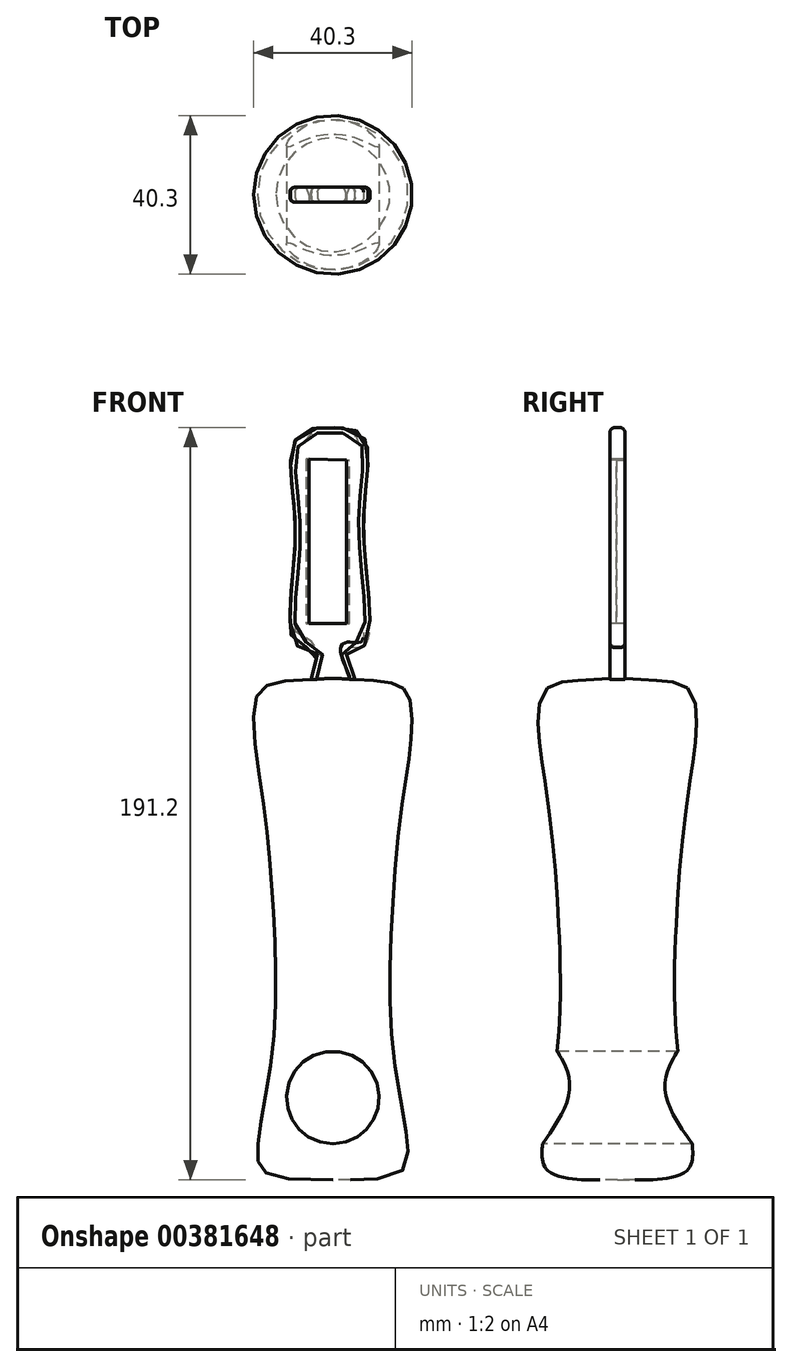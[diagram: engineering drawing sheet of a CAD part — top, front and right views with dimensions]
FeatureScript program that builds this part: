
annotation { "Feature Type Name" : "Feature", "Feature Type Description" : "" }
export const myFeature = defineFeature(function(context is Context, id is Id, definition is map)
    precondition{}
    {
        {
            var Q0;
            Q0=qCreatedBy(makeId("Front.planeOp"),FACE);
            var sketch = newSketch(context, id + "F0", { "sketchPlane" : qUnion([Q0])});
            skFitSpline(sketch, "E0", {"points": [v(0, -68.68) * mm, v(-19.14, -62) * mm, v(-15.4, -36.55) * mm, v(-15.14, 0) * mm, v(-17.89, 28.81) * mm, v(-18.89, 55) * mm, v(0, 58.9) * mm], "startDerivative": vector(-345.44, -10.16) * mm, "endDerivative": vector(220.82, 24.2) * mm});
            skLineSegment(sketch, "E1", {"start": v(0, 58.9) * mm, "end": v(0, -68.68) * mm});
            skSolve(sketch);
        }
        {
            var Q0;
            Q0=qCreatedBy(makeId("Front.planeOp"),FACE);
            var sketch = newSketch(context, id + "F1", { "sketchPlane" : qUnion([Q0])});
            skLineSegment(sketch, "E2", {"start": v(0, 73.34) * mm, "end": v(0, -74.45) * mm, "construction": true});
            skSolve(sketch);
        }
        {
            var Q0;
            Q0=qCreatedBy(makeId("Front.planeOp"),FACE);
            var sketch = newSketch(context, id + "F2", { "sketchPlane" : qUnion([Q0])});
            skCircle(sketch, "E3", {"center": v(0, -47.78) * mm, "radius": 11.77 * mm});
            skSolve(sketch);
        }
        {
            var Q0;
            Q0=qCreatedBy(makeId("Front.planeOp"),FACE);
            var sketch = newSketch(context, id + "F3", { "sketchPlane" : qUnion([Q0])});
            skFitSpline(sketch, "E4", {"points": [v(-5.49, 58.45) * mm, v(-4.16, 66.56) * mm, v(-9.2, 67.02) * mm, v(-9.58, 93.75) * mm, v(-10.76, 113.63) * mm, v(-8.05, 121.04) * mm, v(-0.51, 122.44) * mm, v(7.26, 120.8) * mm, v(8.91, 112.92) * mm, v(7.92, 93.56) * mm, v(7.77, 66.87) * mm, v(3.35, 66.45) * mm, v(5.65, 58.44) * mm], "startDerivative": vector(13.61, 100.7) * mm, "endDerivative": vector(15.57, -108.97) * mm});
            skLineSegment(sketch, "E5", {"start": v(-5.49, 58.45) * mm, "end": v(5.65, 58.44) * mm});
            skSolve(sketch);
        }
        {
            var Q0;
            Q0=makeQuery(id+"F0.imprint","IMPRINT",FACE,{"disambiguationData":[TD([[makeQuery(id+"F0.imprint","IMPRINT",EDGE,{"derivedFrom":sQuery(id+"F0.wireOp",EDGE,"E0")}),-1.0]])]});
            var Q1;
            Q1=sQuery(id+"F1.wireOp",EDGE,"E2");
            revolve(context, id + "F4", {"entities" : qUnion([Q0]), "axis" : qUnion([Q1]), "revolveType" : RevolveType.FULL});
        }
        {
            var Q0;
            Q0=makeQuery(id+"F2.imprint","IMPRINT",FACE,{"disambiguationData":[TD([[makeQuery(id+"F2.imprint","IMPRINT",EDGE,{"derivedFrom":sQuery(id+"F2.wireOp",EDGE,"E3")}),1.0]])]});
            extrude(context, id + "F5", {"entities" : qUnion([Q0]), "operationType" : NewBodyOperationType.REMOVE, "endBound" : BoundingType.SYMMETRIC, "oppositeDirection" : true, "depth" : 127 * mm});
        }
        {
            var Q0;
            Q0=makeQuery(id+"F3.imprint","IMPRINT",FACE,{"disambiguationData":[TD([[makeQuery(id+"F3.imprint","IMPRINT",EDGE,{"derivedFrom":sQuery(id+"F3.wireOp",EDGE,"E4")}),-1.0]])]});
            extrude(context, id + "F6", {"entities" : qUnion([Q0]), "operationType" : NewBodyOperationType.ADD, "endBound" : BoundingType.SYMMETRIC, "depth" : 3.8 * mm});
        }
        {
            var Q0;
            Q0=qCreatedBy(makeId("Front.planeOp"),FACE);
            var sketch = newSketch(context, id + "F7", { "sketchPlane" : qUnion([Q0])});
            skLineSegment(sketch, "E6", {"start": v(-6.09, 114.44) * mm, "end": v(-6.09, 72.7) * mm});
            skLineSegment(sketch, "E7", {"start": v(-6.09, 72.7) * mm, "end": v(3.48, 72.7) * mm});
            skLineSegment(sketch, "E8", {"start": v(3.48, 72.7) * mm, "end": v(3.48, 114.15) * mm});
            skLineSegment(sketch, "E9", {"start": v(3.48, 114.15) * mm, "end": v(-6.09, 114.44) * mm});
            skSolve(sketch);
        }
        {
            var Q0;
            Q0 = qSketchRegion(id + "F7", true);
            extrude(context, id + "F8", {"entities" : qUnion([Q0]), "operationType" : NewBodyOperationType.REMOVE, "endBound" : BoundingType.SYMMETRIC, "oppositeDirection" : true, "depth" : 50.8 * mm});
        }
        {
            var Q0;
            Q0=makeQuery(id+"F6.opExtrude","CAP_EDGE",EDGE,{"disambiguationData":[OSD([sQuery(id+"F3.wireOp",EDGE,"E4")])],"isStart":false});
            var Q1;
            Q1=makeQuery(id+"F6.opExtrude","CAP_EDGE",EDGE,{"disambiguationData":[OSD([sQuery(id+"F3.wireOp",EDGE,"E4")])],"isStart":true});
            fillet(context, id + "F9", {"entities" : qUnion([Q0, Q1]), "radius" : 1.27 * mm, "tangentPropagation" : true, "allowEdgeOverflow" : false});
        }
        {
            var Q0;
            Q0=makeQuery(id+"F8.boolean.opBoolean","INTERSECT",EDGE,{"derivedFrom":[makeQuery(id+"F6.opExtrude","CAP_FACE",FACE,{"disambiguationData":[OSD([sQuery(id+"F3.wireOp",EDGE,"E4"),sQuery(id+"F3.wireOp",EDGE,"E5")])],"isStart":true}),makeQuery(id+"F8.opExtrude","SWEPT_FACE",FACE,{"disambiguationData":[OSD([sQuery(id+"F7.wireOp",EDGE,"E6")])]})]});
            var Q1;
            Q1=makeQuery(id+"F8.boolean.opBoolean","INTERSECT",EDGE,{"derivedFrom":[makeQuery(id+"F6.opExtrude","CAP_FACE",FACE,{"disambiguationData":[OSD([sQuery(id+"F3.wireOp",EDGE,"E4"),sQuery(id+"F3.wireOp",EDGE,"E5")])],"isStart":true}),makeQuery(id+"F8.opExtrude","SWEPT_FACE",FACE,{"disambiguationData":[OSD([sQuery(id+"F7.wireOp",EDGE,"E8")])]})]});
            chamfer(context, id + "F10", {"entities" : qUnion([Q0, Q1]), "chamferType" : ChamferType.OFFSET_ANGLE, "width" : 0.76 * mm, "oppositeDirection" : false, "angle" : 70 * degree, "tangentPropagation" : true});
        }
    });
